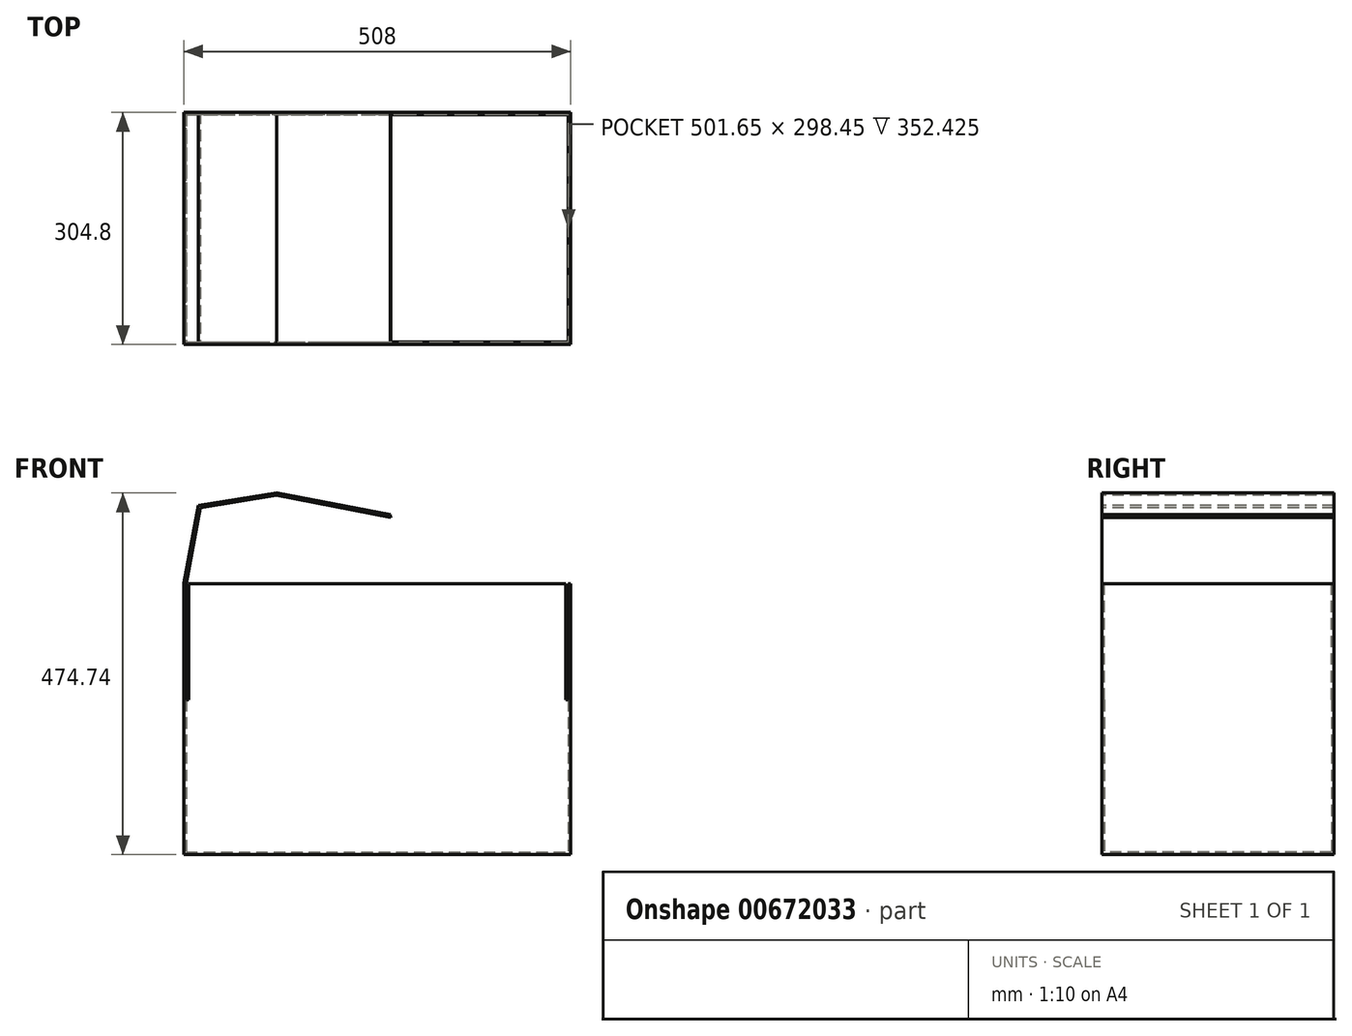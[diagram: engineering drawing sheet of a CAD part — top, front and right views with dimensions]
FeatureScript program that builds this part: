
annotation { "Feature Type Name" : "Feature", "Feature Type Description" : "" }
export const myFeature = defineFeature(function(context is Context, id is Id, definition is map)
    precondition{}
    {
        {
            var Q0;
            Q0=qCreatedBy(makeId("Top.planeOp"),FACE);
            var sketch = newSketch(context, id + "F0", { "sketchPlane" : qUnion([Q0])});
            skLineSegment(sketch, "E0.bottom", {"start": v(-254, 152.4) * mm, "end": v(254, 152.4) * mm});
            skLineSegment(sketch, "E0.top", {"start": v(-254, -152.4) * mm, "end": v(254, -152.4) * mm});
            skLineSegment(sketch, "E0.left", {"start": v(-254, 152.4) * mm, "end": v(-254, -152.4) * mm});
            skLineSegment(sketch, "E0.right", {"start": v(254, 152.4) * mm, "end": v(254, -152.4) * mm});
            skPoint(sketch, "E0.middle", {"position": v(0, 0) * mm});
            skSolve(sketch);
        }
        {
            var Q0;
            Q0 = qSketchRegion(id + "F0", true);
            extrude(context, id + "F1", {"entities" : qUnion([Q0]), "depth" : 355.6 * mm, "offsetDistance" : 25.4 * mm});
        }
        {
            var Q0;
            Q0=makeQuery(id+"F1.opExtrude","CAP_FACE",FACE,{"disambiguationData":[OSD([sQuery(id+"F0.wireOp",EDGE,"E0.bottom"),sQuery(id+"F0.wireOp",EDGE,"E0.top"),sQuery(id+"F0.wireOp",EDGE,"E0.left"),sQuery(id+"F0.wireOp",EDGE,"E0.right")])],"isStart":false});
            shell(context, id + "F2", {"entities" : qUnion([Q0]), "thickness" : 3.17 * mm});
        }
        {
            var Q0;
            Q0=makeQuery(id+"F1.opExtrude","SWEPT_FACE",FACE,{"disambiguationData":[OSD([sQuery(id+"F0.wireOp",EDGE,"E0.top")])]});
            var sketch = newSketch(context, id + "F3", { "sketchPlane" : qUnion([Q0])});
            skLineSegment(sketch, "E1", {"start": v(-247.65, 355.6) * mm, "end": v(-247.65, 203.2) * mm});
            skLineSegment(sketch, "E2", {"start": v(-247.65, 203.2) * mm, "end": v(-250.83, 203.2) * mm});
            skLineSegment(sketch, "E3", {"start": v(-250.83, 203.2) * mm, "end": v(-250.83, 355.6) * mm});
            skLineSegment(sketch, "E4", {"start": v(-250.83, 355.6) * mm, "end": v(-247.65, 355.6) * mm});
            skLineSegment(sketch, "E5", {"start": v(0, 0) * mm, "end": v(0, 355.6) * mm, "construction": true});
            skLineSegment(sketch, "E6.MirrorCS", {"start": v(250.83, 355.6) * mm, "end": v(247.65, 355.6) * mm});
            skLineSegment(sketch, "E7.MirrorCS", {"start": v(247.65, 203.2) * mm, "end": v(250.83, 203.2) * mm});
            skLineSegment(sketch, "E8.MirrorCS", {"start": v(247.65, 355.6) * mm, "end": v(247.65, 203.2) * mm});
            skLineSegment(sketch, "E9.MirrorCS", {"start": v(250.83, 203.2) * mm, "end": v(250.83, 355.6) * mm});
            skSolve(sketch);
        }
        {
            var Q0;
            Q0 = qSketchRegion(id + "F3", true);
            extrude(context, id + "F4", {"entities" : qUnion([Q0]), "operationType" : NewBodyOperationType.REMOVE, "endBound" : BoundingType.THROUGH_ALL, "oppositeDirection" : true, "depth" : 25.4 * mm, "offsetDistance" : 25.4 * mm});
        }
        {
            var Q0;
            Q0=makeQuery(id+"F1.opExtrude","SWEPT_FACE",FACE,{"disambiguationData":[OSD([sQuery(id+"F0.wireOp",EDGE,"E0.top")])]});
            var sketch = newSketch(context, id + "F5", { "sketchPlane" : qUnion([Q0])});
            skLineSegment(sketch, "E10", {"start": v(-250.83, 355.6) * mm, "end": v(-232.1, 455.46) * mm});
            skLineSegment(sketch, "E11", {"start": v(-232.1, 455.46) * mm, "end": v(-131.78, 471.51) * mm});
            skLineSegment(sketch, "E12", {"start": v(-131.78, 471.51) * mm, "end": v(17.86, 442.67) * mm});
            skLineSegment(sketch, "E13.0", {"start": v(-131.73, 474.74) * mm, "end": v(16.93, 446.08) * mm});
            skLineSegment(sketch, "E13.1", {"start": v(-234.82, 458.24) * mm, "end": v(-131.73, 474.74) * mm});
            skLineSegment(sketch, "E13.2", {"start": v(-253.95, 356.18) * mm, "end": v(-234.82, 458.24) * mm});
            skLineSegment(sketch, "E14", {"start": v(17.86, 442.67) * mm, "end": v(16.93, 446.08) * mm});
            skLineSegment(sketch, "E15", {"start": v(-253.95, 356.18) * mm, "end": v(-254, 355.6) * mm});
            skLineSegment(sketch, "E16", {"start": v(-254, 355.6) * mm, "end": v(-250.83, 355.6) * mm});
            skSolve(sketch);
        }
        {
            var Q0;
            Q0 = qSketchRegion(id + "F5", true);
            extrude(context, id + "F6", {"entities" : qUnion([Q0]), "oppositeDirection" : true, "depth" : 304.8 * mm, "offsetDistance" : 25.4 * mm});
        }
    });
